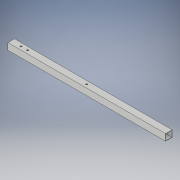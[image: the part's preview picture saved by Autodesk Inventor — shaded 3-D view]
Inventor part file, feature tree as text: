
AUTODESK INVENTOR PART (.ipt)
format: ipt  version: 2017 (Build 210142000, 142)  size: 113,664 bytes
history: native  units: in
note: dims shown in document units (in); Inventor stores cm internally (conversion verified against a paired STEP export)
features: extrude x2, sketch x2
ambient origin geometry x8: Origin, YZ Plane, XZ Plane, XY Plane, X Axis, Y Axis, Z Axis, Center Point
bodies: Solid1 (feature_tree)
feature tree (4):
  extrude  "Extrusion1"  Depth=1.0in
  extrude  "Extrusion2"  Depth=24.0in TaperAngle=0.0deg
  sketch  "Sketch1"  dims[d0=1.0in d1=1.0in]
  sketch  "Sketch2"  dims[d2=0.0625in d3=24.0in d4=0.0in d5=0.25in d6=1.5in d7=2.5in d8=11.5in d9=1.0in d10=0.0in]
